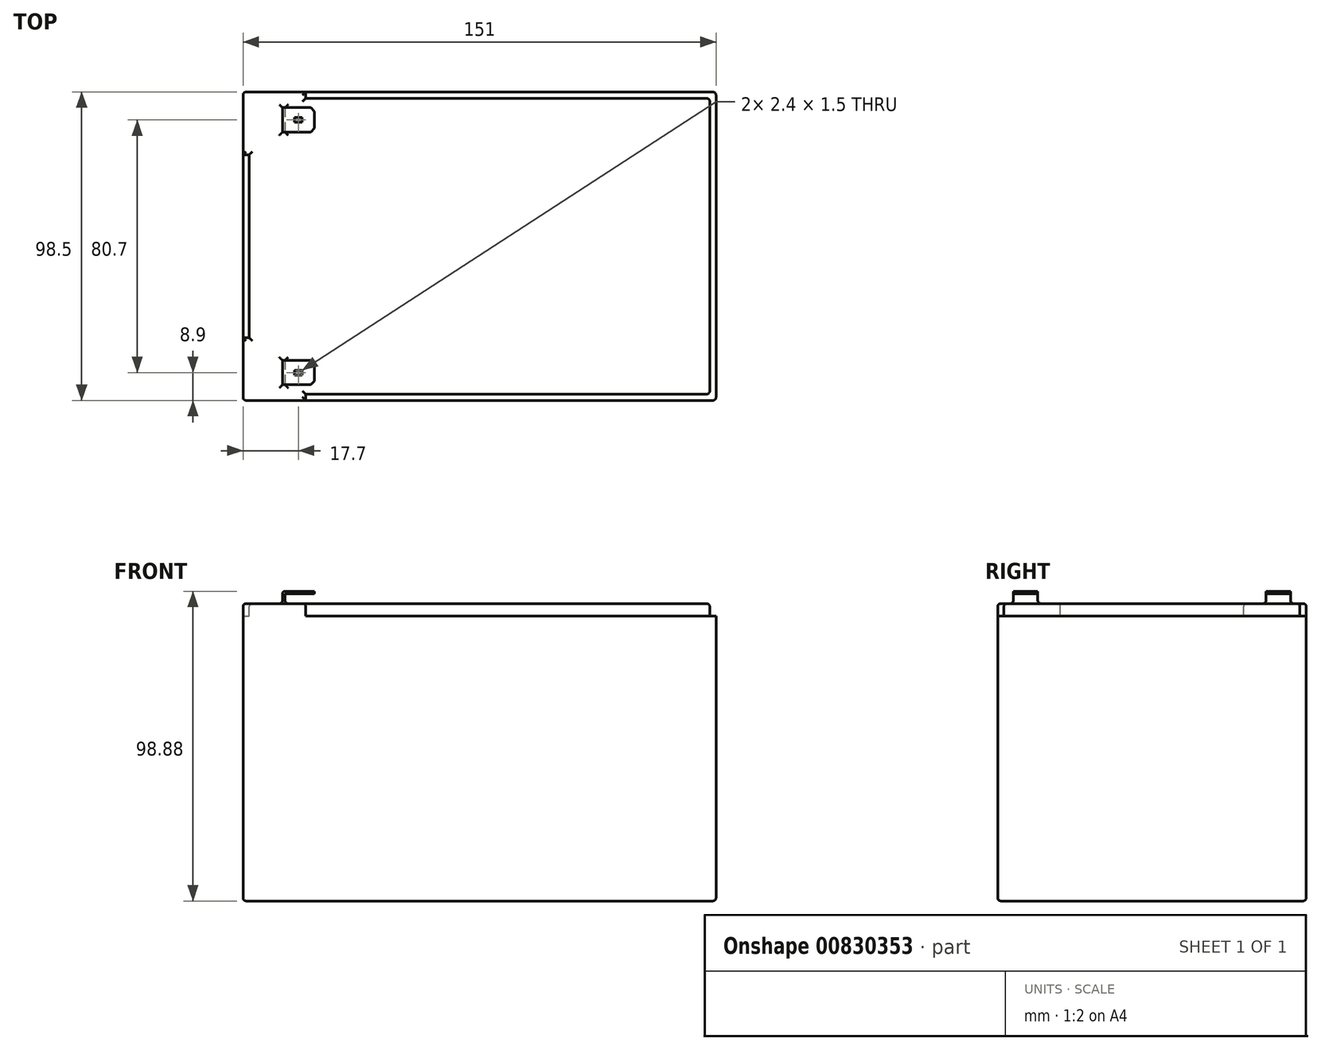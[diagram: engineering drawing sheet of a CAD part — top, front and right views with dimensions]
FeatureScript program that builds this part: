
annotation { "Feature Type Name" : "Feature", "Feature Type Description" : "" }
export const myFeature = defineFeature(function(context is Context, id is Id, definition is map)
    precondition{}
    {
        {
            var Q0;
            Q0=qCreatedBy(makeId("Top.planeOp"),FACE);
            var sketch = newSketch(context, id + "F0", { "sketchPlane" : qUnion([Q0])});
            skLineSegment(sketch, "E0.bottom", {"start": v(-75.5, -49.25) * mm, "end": v(75.5, -49.25) * mm});
            skLineSegment(sketch, "E0.top", {"start": v(-75.5, 49.25) * mm, "end": v(75.5, 49.25) * mm});
            skLineSegment(sketch, "E0.left", {"start": v(-75.5, -49.25) * mm, "end": v(-75.5, 49.25) * mm});
            skLineSegment(sketch, "E0.right", {"start": v(75.5, -49.25) * mm, "end": v(75.5, 49.25) * mm});
            skPoint(sketch, "E0.middle", {"position": v(0, 0) * mm});
            skSolve(sketch);
        }
        {
            var Q0;
            Q0=makeQuery(id+"F0.imprint","IMPRINT",FACE,{"disambiguationData":[TD([[makeQuery(id+"F0.imprint","IMPRINT",EDGE,{"derivedFrom":sQuery(id+"F0.wireOp",EDGE,"E0.bottom")}),1.0]])]});
            extrude(context, id + "F1", {"entities" : qUnion([Q0]), "depth" : 95 * mm, "offsetDistance" : 25 * mm});
        }
        {
            var Q0;
            Q0=makeQuery(id+"F1.opExtrude","CAP_FACE",FACE,{"disambiguationData":[OSD([sQuery(id+"F0.wireOp",EDGE,"E0.bottom"),sQuery(id+"F0.wireOp",EDGE,"E0.top"),sQuery(id+"F0.wireOp",EDGE,"E0.left"),sQuery(id+"F0.wireOp",EDGE,"E0.right")])],"isStart":false});
            var sketch = newSketch(context, id + "F2", { "sketchPlane" : qUnion([Q0])});
            skLineSegment(sketch, "E1", {"start": v(-75.5, -29.25) * mm, "end": v(-73.5, -29.25) * mm});
            skLineSegment(sketch, "E2", {"start": v(-55.5, -47.25) * mm, "end": v(-55.5, -49.25) * mm});
            skLineSegment(sketch, "E3", {"start": v(-75.5, 0) * mm, "end": v(75.5, 0) * mm, "construction": true});
            skLineSegment(sketch, "E4.MirrorCS", {"start": v(-75.5, 29.25) * mm, "end": v(-73.5, 29.25) * mm});
            skLineSegment(sketch, "E5", {"start": v(75.5, 0) * mm, "end": v(73.5, 0) * mm});
            skLineSegment(sketch, "E6", {"start": v(73.5, 0) * mm, "end": v(73.5, -47.25) * mm});
            skLineSegment(sketch, "E7", {"start": v(73.5, -47.25) * mm, "end": v(-55.5, -47.25) * mm});
            skLineSegment(sketch, "E8", {"start": v(-73.5, -29.25) * mm, "end": v(-73.5, 29.25) * mm});
            skLineSegment(sketch, "E9.MirrorCS", {"start": v(73.5, 47.25) * mm, "end": v(-55.5, 47.25) * mm});
            skLineSegment(sketch, "E10.MirrorCS", {"start": v(73.5, 0) * mm, "end": v(73.5, 47.25) * mm});
            skLineSegment(sketch, "E11.MirrorCS", {"start": v(-55.5, 47.25) * mm, "end": v(-55.5, 49.25) * mm});
            skSolve(sketch);
        }
        {
            var Q0;
            {var subQ1=sQuery(id+"F2.wireOp",EDGE,"E2");Q0=makeQuery(id+"F2.imprint","IMPRINT",FACE,{"disambiguationData":[TD([[makeQuery(id+"F2.imprint","IMPRINT",EDGE,{"derivedFrom":subQ1}),1.0]])]});}
            var Q1;
            {var subQ4=sQuery(id+"F2.wireOp",EDGE,"E5");Q1=makeQuery(id+"F2.imprint","IMPRINT",FACE,{"disambiguationData":[TD([[makeQuery(id+"F2.imprint","IMPRINT",EDGE,{"derivedFrom":subQ4}),-1.0]])]});}
            var Q2;
            {var subQ0=sQuery(id+"F2.wireOp",EDGE,"E1");Q2=makeQuery(id+"F2.imprint","IMPRINT",FACE,{"disambiguationData":[TD([[makeQuery(id+"F2.imprint","IMPRINT",EDGE,{"derivedFrom":subQ0}),1.0]])]});}
            extrude(context, id + "F3", {"entities" : qUnion([Q0, Q1, Q2]), "operationType" : NewBodyOperationType.REMOVE, "oppositeDirection" : true, "depth" : 4 * mm, "offsetDistance" : 25 * mm});
        }
        {
            var Q0;
            Q0=makeQuery(id+"F1.opExtrude","CAP_FACE",FACE,{"disambiguationData":[OSD([sQuery(id+"F0.wireOp",EDGE,"E0.bottom"),sQuery(id+"F0.wireOp",EDGE,"E0.top"),sQuery(id+"F0.wireOp",EDGE,"E0.left"),sQuery(id+"F0.wireOp",EDGE,"E0.right")])],"isStart":false});
            var sketch = newSketch(context, id + "F4", { "sketchPlane" : qUnion([Q0])});
            skLineSegment(sketch, "E12", {"start": v(-62.9, -49.25) * mm, "end": v(-62.9, -44.25) * mm, "construction": true});
            skLineSegment(sketch, "E13", {"start": v(-62.9, -44.25) * mm, "end": v(-75.5, -44.25) * mm, "construction": true});
            skLineSegment(sketch, "E14.bottom", {"start": v(-62.9, -44.25) * mm, "end": v(-52.7, -44.25) * mm});
            skLineSegment(sketch, "E14.top", {"start": v(-62.9, -36.45) * mm, "end": v(-52.7, -36.45) * mm});
            skLineSegment(sketch, "E14.left", {"start": v(-62.9, -44.25) * mm, "end": v(-62.9, -36.45) * mm});
            skLineSegment(sketch, "E14.right", {"start": v(-52.7, -44.25) * mm, "end": v(-52.7, -36.45) * mm});
            skLineSegment(sketch, "E15", {"start": v(73.5, 0) * mm, "end": v(-73.5, 0) * mm, "construction": true});
            skLineSegment(sketch, "E16.MirrorCS", {"start": v(-62.9, 49.25) * mm, "end": v(-62.9, 44.25) * mm, "construction": true});
            skLineSegment(sketch, "E17.MirrorCS", {"start": v(-62.9, 44.25) * mm, "end": v(-75.5, 44.25) * mm, "construction": true});
            skLineSegment(sketch, "E18.MirrorCS", {"start": v(-62.9, 44.25) * mm, "end": v(-62.9, 36.45) * mm});
            skLineSegment(sketch, "E19.MirrorCS", {"start": v(-62.9, 36.45) * mm, "end": v(-52.7, 36.45) * mm});
            skLineSegment(sketch, "E20.MirrorCS", {"start": v(-62.9, 44.25) * mm, "end": v(-52.7, 44.25) * mm});
            skLineSegment(sketch, "E21.MirrorCS", {"start": v(-52.7, 44.25) * mm, "end": v(-52.7, 36.45) * mm});
            skSolve(sketch);
        }
        {
            var Q0;
            Q0=makeQuery(id+"F4.imprint","IMPRINT",FACE,{"disambiguationData":[TD([[makeQuery(id+"F4.imprint","IMPRINT",EDGE,{"derivedFrom":sQuery(id+"F4.wireOp",EDGE,"E14.bottom")}),1.0]])]});
            var Q1;
            Q1=makeQuery(id+"F4.imprint","IMPRINT",FACE,{"disambiguationData":[TD([[makeQuery(id+"F4.imprint","IMPRINT",EDGE,{"derivedFrom":sQuery(id+"F4.wireOp",EDGE,"E18.MirrorCS")}),1.0]])]});
            extrude(context, id + "F5", {"entities" : qUnion([Q0, Q1]), "operationType" : NewBodyOperationType.ADD, "depth" : 3.88 * mm, "offsetDistance" : 25 * mm});
        }
        {
            var Q0;
            Q0=makeQuery(id+"F5.opExtrude","SWEPT_FACE",FACE,{"disambiguationData":[OSD([sQuery(id+"F4.wireOp",EDGE,"E14.bottom")])]});
            var sketch = newSketch(context, id + "F6", { "sketchPlane" : qUnion([Q0])});
            skLineSegment(sketch, "E22", {"start": v(-62.1, 95) * mm, "end": v(-62.1, 97.78) * mm});
            skLineSegment(sketch, "E23", {"start": v(-61.8, 98.08) * mm, "end": v(-52.7, 98.08) * mm});
            skPoint(sketch, "E24.visualSharp", {"position": v(-62.1, 98.08) * mm});
            skArc(sketch, "E24.filletArc", {"start": v(-61.8, 98.08) * mm, "mid": v(-62.01, 98) * mm, "end": v(-62.1, 97.78) * mm});
            skSolve(sketch);
        }
        {
            var Q0;
            {var subQ5=sQuery(id+"F6.wireOp",EDGE,"E22");Q0=makeQuery(id+"F6.imprint","IMPRINT",FACE,{"disambiguationData":[TD([[makeQuery(id+"F6.imprint","IMPRINT",EDGE,{"derivedFrom":subQ5}),-1.0]])]});}
            extrude(context, id + "F7", {"entities" : qUnion([Q0]), "operationType" : NewBodyOperationType.REMOVE, "endBound" : BoundingType.THROUGH_ALL, "oppositeDirection" : true, "depth" : 25 * mm, "offsetDistance" : 25 * mm});
        }
        {
            var Q0;
            Q0=makeQuery(id+"F5.opExtrude","CAP_FACE",FACE,{"disambiguationData":[OSD([sQuery(id+"F4.wireOp",EDGE,"E18.MirrorCS"),sQuery(id+"F4.wireOp",EDGE,"E19.MirrorCS"),sQuery(id+"F4.wireOp",EDGE,"E20.MirrorCS"),sQuery(id+"F4.wireOp",EDGE,"E21.MirrorCS")])],"isStart":false});
            var sketch = newSketch(context, id + "F8", { "sketchPlane" : qUnion([Q0])});
            skLineSegment(sketch, "E25.bottom", {"start": v(-59, 41.1) * mm, "end": v(-56.6, 41.1) * mm});
            skLineSegment(sketch, "E25.top", {"start": v(-59, 39.6) * mm, "end": v(-56.6, 39.6) * mm});
            skLineSegment(sketch, "E25.left", {"start": v(-59, 41.1) * mm, "end": v(-59, 39.6) * mm});
            skLineSegment(sketch, "E25.right", {"start": v(-56.6, 41.1) * mm, "end": v(-56.6, 39.6) * mm});
            skPoint(sketch, "E25.middle", {"position": v(-57.8, 40.35) * mm});
            skPoint(sketch, "E25.middle.positionSnap0", {"position": v(-57.8, 44.25) * mm});
            skPoint(sketch, "E25.middle.positionSnap1", {"position": v(-52.7, 40.35) * mm});
            skPoint(sketch, "E25.centerSnap0", {"position": v(-57.8, 44.25) * mm});
            skPoint(sketch, "E25.centerSnap1", {"position": v(-52.7, 40.35) * mm});
            skSolve(sketch);
        }
        {
            var Q0;
            Q0=makeQuery(id+"F8.imprint","IMPRINT",FACE,{"disambiguationData":[TD([[makeQuery(id+"F8.imprint","IMPRINT",EDGE,{"derivedFrom":sQuery(id+"F8.wireOp",EDGE,"E25.bottom")}),-1.0]])]});
            extrude(context, id + "F9", {"entities" : qUnion([Q0]), "operationType" : NewBodyOperationType.REMOVE, "endBound" : BoundingType.UP_TO_NEXT, "oppositeDirection" : true, "depth" : 25 * mm, "offsetDistance" : 25 * mm});
        }
        {
            var Q0;
            Q0=makeQuery(id+"F5.opExtrude","CAP_FACE",FACE,{"disambiguationData":[OSD([sQuery(id+"F4.wireOp",EDGE,"E14.bottom"),sQuery(id+"F4.wireOp",EDGE,"E14.top"),sQuery(id+"F4.wireOp",EDGE,"E14.left"),sQuery(id+"F4.wireOp",EDGE,"E14.right")])],"isStart":false});
            var sketch = newSketch(context, id + "F10", { "sketchPlane" : qUnion([Q0])});
            skLineSegment(sketch, "E26.bottom", {"start": v(-59, -41.1) * mm, "end": v(-56.6, -41.1) * mm});
            skLineSegment(sketch, "E26.top", {"start": v(-59, -39.6) * mm, "end": v(-56.6, -39.6) * mm});
            skLineSegment(sketch, "E26.left", {"start": v(-59, -41.1) * mm, "end": v(-59, -39.6) * mm});
            skLineSegment(sketch, "E26.right", {"start": v(-56.6, -41.1) * mm, "end": v(-56.6, -39.6) * mm});
            skPoint(sketch, "E26.middle", {"position": v(-57.8, -40.35) * mm});
            skPoint(sketch, "E26.middle.positionSnap0", {"position": v(-57.8, -36.45) * mm});
            skPoint(sketch, "E26.middle.positionSnap1", {"position": v(-52.7, -40.35) * mm});
            skPoint(sketch, "E26.centerSnap0", {"position": v(-57.8, -36.45) * mm});
            skPoint(sketch, "E26.centerSnap1", {"position": v(-52.7, -40.35) * mm});
            skSolve(sketch);
        }
        {
            var Q0;
            Q0=makeQuery(id+"F10.imprint","IMPRINT",FACE,{"disambiguationData":[TD([[makeQuery(id+"F10.imprint","IMPRINT",EDGE,{"derivedFrom":sQuery(id+"F10.wireOp",EDGE,"E26.bottom")}),1.0]])]});
            extrude(context, id + "F11", {"entities" : qUnion([Q0]), "operationType" : NewBodyOperationType.REMOVE, "oppositeDirection" : true, "depth" : 2 * mm, "offsetDistance" : 25 * mm});
        }
        {
            var Q0;
            Q0=makeQuery(id+"F5.opExtrude","SWEPT_EDGE",EDGE,{"disambiguationData":[OSD([sQuery(id+"F4.wireOp",EDGE,"E14.bottom"),sQuery(id+"F4.wireOp",EDGE,"E14.right")])]});
            var Q1;
            Q1=makeQuery(id+"F5.opExtrude","SWEPT_EDGE",EDGE,{"disambiguationData":[OSD([sQuery(id+"F4.wireOp",EDGE,"E14.top"),sQuery(id+"F4.wireOp",EDGE,"E14.right")])]});
            var Q2;
            Q2=makeQuery(id+"F5.opExtrude","SWEPT_EDGE",EDGE,{"disambiguationData":[OSD([sQuery(id+"F4.wireOp",EDGE,"E19.MirrorCS"),sQuery(id+"F4.wireOp",EDGE,"E21.MirrorCS")])]});
            var Q3;
            Q3=makeQuery(id+"F5.opExtrude","SWEPT_EDGE",EDGE,{"disambiguationData":[OSD([sQuery(id+"F4.wireOp",EDGE,"E20.MirrorCS"),sQuery(id+"F4.wireOp",EDGE,"E21.MirrorCS")])]});
            chamfer(context, id + "F12", {"entities" : qUnion([Q0, Q1, Q2, Q3]), "width" : 1.2 * mm, "tangentPropagation" : true});
        }
        {
            var Q0;
            Q0=makeQuery(id+"F5.opExtrude","CAP_EDGE",EDGE,{"disambiguationData":[OSD([sQuery(id+"F4.wireOp",EDGE,"E14.left")])],"isStart":false});
            var Q1;
            Q1=makeQuery(id+"F5.opExtrude","CAP_EDGE",EDGE,{"disambiguationData":[OSD([sQuery(id+"F4.wireOp",EDGE,"E18.MirrorCS")])],"isStart":false});
            fillet(context, id + "F13", {"entities" : qUnion([Q0, Q1]), "radius" : 0.7 * mm, "tangentPropagation" : true, "allowEdgeOverflow" : false});
        }
        {
            var Q0;
            Q0=makeQuery(id+"F3.boolean.opBoolean","COPY",EDGE,{"derivedFrom":makeQuery(id+"F3.opExtrude","CAP_EDGE",EDGE,{"disambiguationData":[OSD([sQuery(id+"F2.wireOp",EDGE,"E6"),sQuery(id+"F2.wireOp",EDGE,"E10.MirrorCS")])],"isStart":true})});
            var Q1;
            Q1=makeQuery(id+"F3.boolean.opBoolean","COPY",EDGE,{"derivedFrom":makeQuery(id+"F3.opExtrude","CAP_EDGE",EDGE,{"disambiguationData":[OSD([sQuery(id+"F2.wireOp",EDGE,"E9.MirrorCS")])],"isStart":true})});
            var Q2;
            Q2=makeQuery(id+"F3.boolean.opBoolean","COPY",EDGE,{"derivedFrom":makeQuery(id+"F3.opExtrude","CAP_EDGE",EDGE,{"disambiguationData":[OSD([sQuery(id+"F0.wireOp",EDGE,"E0.top")])],"isStart":false})});
            var Q3;
            Q3=makeQuery(id+"F3.boolean.opBoolean","COPY",EDGE,{"derivedFrom":makeQuery(id+"F3.opExtrude","CAP_EDGE",EDGE,{"disambiguationData":[OSD([sQuery(id+"F0.wireOp",EDGE,"E0.right")])],"isStart":false})});
            var Q4;
            Q4=makeQuery(id+"F1.opExtrude","SWEPT_EDGE",EDGE,{"disambiguationData":[OSD([sQuery(id+"F0.wireOp",EDGE,"E0.top"),sQuery(id+"F0.wireOp",EDGE,"E0.right")])]});
            var Q5;
            Q5=makeQuery(id+"F3.boolean.opBoolean","COPY",EDGE,{"derivedFrom":makeQuery(id+"F3.opExtrude","SWEPT_EDGE",EDGE,{"disambiguationData":[OSD([sQuery(id+"F2.wireOp",EDGE,"E9.MirrorCS"),sQuery(id+"F2.wireOp",EDGE,"E10.MirrorCS")])]})});
            var Q6;
            Q6=makeQuery(id+"F1.opExtrude","SWEPT_EDGE",EDGE,{"disambiguationData":[OSD([sQuery(id+"F0.wireOp",EDGE,"E0.bottom"),sQuery(id+"F0.wireOp",EDGE,"E0.right")])]});
            var Q7;
            Q7=makeQuery(id+"F1.opExtrude","CAP_EDGE",EDGE,{"disambiguationData":[OSD([sQuery(id+"F0.wireOp",EDGE,"E0.right")])],"isStart":true});
            var Q8;
            Q8=makeQuery(id+"F1.opExtrude","CAP_EDGE",EDGE,{"disambiguationData":[OSD([sQuery(id+"F0.wireOp",EDGE,"E0.top")])],"isStart":true});
            var Q9;
            Q9=makeQuery(id+"F1.opExtrude","SWEPT_EDGE",EDGE,{"disambiguationData":[OSD([sQuery(id+"F0.wireOp",EDGE,"E0.top"),sQuery(id+"F0.wireOp",EDGE,"E0.left")])]});
            var Q10;
            Q10=makeQuery(id+"F1.opExtrude","CAP_EDGE",EDGE,{"disambiguationData":[OSD([sQuery(id+"F0.wireOp",EDGE,"E0.top")])],"isStart":false});
            var Q11;
            Q11=makeQuery(id+"F3.boolean.opBoolean","COPY",EDGE,{"derivedFrom":makeQuery(id+"F3.opExtrude","CAP_EDGE",EDGE,{"disambiguationData":[OSD([sQuery(id+"F2.wireOp",EDGE,"E11.MirrorCS")])],"isStart":true})});
            var Q12;
            Q12=makeQuery(id+"F3.boolean.opBoolean","COPY",EDGE,{"derivedFrom":makeQuery(id+"F3.opExtrude","SWEPT_EDGE",EDGE,{"disambiguationData":[OSD([sQuery(id+"F0.wireOp",EDGE,"E0.top"),sQuery(id+"F2.wireOp",EDGE,"E11.MirrorCS")])]})});
            var Q13;
            {var subQ0=sQuery(id+"F0.wireOp",EDGE,"E0.left");var subQ1=sQuery(id+"F0.wireOp",EDGE,"E0.top");Q13=makeQuery(id+"F3.boolean.opBoolean","SPLIT",EDGE,{"disambiguationData":[TD([makeQuery(id+"F1.opExtrude","SWEPT_FACE",FACE,{"disambiguationData":[OSD([subQ1])]})])],"derivedFrom":makeQuery(id+"F1.opExtrude","CAP_EDGE",EDGE,{"disambiguationData":[OSD([subQ0])],"isStart":false})});}
            var Q14;
            Q14=makeQuery(id+"F3.boolean.opBoolean","COPY",EDGE,{"derivedFrom":makeQuery(id+"F3.opExtrude","CAP_EDGE",EDGE,{"disambiguationData":[OSD([sQuery(id+"F2.wireOp",EDGE,"E8")])],"isStart":true})});
            var Q15;
            Q15=makeQuery(id+"F3.boolean.opBoolean","COPY",EDGE,{"derivedFrom":makeQuery(id+"F3.opExtrude","CAP_EDGE",EDGE,{"disambiguationData":[OSD([sQuery(id+"F0.wireOp",EDGE,"E0.left")])],"isStart":false})});
            var Q16;
            {var subQ0=sQuery(id+"F0.wireOp",EDGE,"E0.bottom");var subQ1=sQuery(id+"F0.wireOp",EDGE,"E0.left");Q16=makeQuery(id+"F3.boolean.opBoolean","SPLIT",EDGE,{"disambiguationData":[TD([makeQuery(id+"F1.opExtrude","SWEPT_FACE",FACE,{"disambiguationData":[OSD([subQ0])]})])],"derivedFrom":makeQuery(id+"F1.opExtrude","CAP_EDGE",EDGE,{"disambiguationData":[OSD([subQ1])],"isStart":false})});}
            var Q17;
            Q17=makeQuery(id+"F1.opExtrude","CAP_EDGE",EDGE,{"disambiguationData":[OSD([sQuery(id+"F0.wireOp",EDGE,"E0.bottom")])],"isStart":false});
            var Q18;
            Q18=makeQuery(id+"F3.boolean.opBoolean","COPY",EDGE,{"derivedFrom":makeQuery(id+"F3.opExtrude","CAP_EDGE",EDGE,{"disambiguationData":[OSD([sQuery(id+"F2.wireOp",EDGE,"E7")])],"isStart":true})});
            var Q19;
            Q19=makeQuery(id+"F1.opExtrude","CAP_EDGE",EDGE,{"disambiguationData":[OSD([sQuery(id+"F0.wireOp",EDGE,"E0.left")])],"isStart":true});
            var Q20;
            Q20=makeQuery(id+"F1.opExtrude","SWEPT_EDGE",EDGE,{"disambiguationData":[OSD([sQuery(id+"F0.wireOp",EDGE,"E0.bottom"),sQuery(id+"F0.wireOp",EDGE,"E0.left")])]});
            var Q21;
            Q21=makeQuery(id+"F1.opExtrude","CAP_EDGE",EDGE,{"disambiguationData":[OSD([sQuery(id+"F0.wireOp",EDGE,"E0.bottom")])],"isStart":true});
            var Q22;
            Q22=makeQuery(id+"F3.boolean.opBoolean","COPY",EDGE,{"derivedFrom":makeQuery(id+"F3.opExtrude","CAP_EDGE",EDGE,{"disambiguationData":[OSD([sQuery(id+"F0.wireOp",EDGE,"E0.bottom")])],"isStart":false})});
            var Q23;
            Q23=makeQuery(id+"F3.boolean.opBoolean","COPY",EDGE,{"derivedFrom":makeQuery(id+"F3.opExtrude","SWEPT_EDGE",EDGE,{"disambiguationData":[OSD([sQuery(id+"F0.wireOp",EDGE,"E0.bottom"),sQuery(id+"F2.wireOp",EDGE,"E2")])]})});
            var Q24;
            Q24=makeQuery(id+"F3.boolean.opBoolean","COPY",EDGE,{"derivedFrom":makeQuery(id+"F3.opExtrude","SWEPT_EDGE",EDGE,{"disambiguationData":[OSD([sQuery(id+"F2.wireOp",EDGE,"E6"),sQuery(id+"F2.wireOp",EDGE,"E7")])]})});
            var Q25;
            Q25=makeQuery(id+"F3.boolean.opBoolean","COPY",EDGE,{"derivedFrom":makeQuery(id+"F3.opExtrude","SWEPT_EDGE",EDGE,{"disambiguationData":[OSD([sQuery(id+"F0.wireOp",EDGE,"E0.left"),sQuery(id+"F2.wireOp",EDGE,"E1")])]})});
            var Q26;
            Q26=makeQuery(id+"F3.boolean.opBoolean","COPY",EDGE,{"derivedFrom":makeQuery(id+"F3.opExtrude","SWEPT_EDGE",EDGE,{"disambiguationData":[OSD([sQuery(id+"F0.wireOp",EDGE,"E0.left"),sQuery(id+"F2.wireOp",EDGE,"E4.MirrorCS")])]})});
            var Q27;
            Q27=makeQuery(id+"F3.boolean.opBoolean","COPY",EDGE,{"derivedFrom":makeQuery(id+"F3.opExtrude","CAP_EDGE",EDGE,{"disambiguationData":[OSD([sQuery(id+"F2.wireOp",EDGE,"E4.MirrorCS")])],"isStart":true})});
            var Q28;
            Q28=makeQuery(id+"F7.boolean.opBoolean","MERGE",FACE,{"derivedFrom":[makeQuery(id+"F1.opExtrude","CAP_FACE",FACE,{"disambiguationData":[OSD([sQuery(id+"F0.wireOp",EDGE,"E0.bottom"),sQuery(id+"F0.wireOp",EDGE,"E0.top"),sQuery(id+"F0.wireOp",EDGE,"E0.left"),sQuery(id+"F0.wireOp",EDGE,"E0.right")])],"isStart":false}),makeQuery(id+"F7.opExtrude","SWEPT_FACE",FACE,{"disambiguationData":[OSD([sQuery(id+"F4.wireOp",EDGE,"E14.bottom")])]})]});
            fillet(context, id + "F14", {"entities" : qUnion([Q0, Q1, Q2, Q3, Q4, Q5, Q6, Q7, Q8, Q9, Q10, Q11, Q12, Q13, Q14, Q15, Q16, Q17, Q18, Q19, Q20, Q21, Q22, Q23, Q24, Q25, Q26, Q27, Q28]), "radius" : 1 * mm, "tangentPropagation" : true, "allowEdgeOverflow" : false});
        }
    });
